# Revit family: LC-3
name_source: partatom
category: Generic Models
revit_build: Autodesk Revit 2017 (Build: 20170419_0315(x64)
units: mm (PartAtom-declared; Revit-internal decimal feet)

## family parameters
Always vertical = Yes
Can host rebar = No
Cut with Voids When Loaded = No
Host = Wall
Part Type = Normal
Room Calculation Point = No
Round Connector Dimension = Use Diameter
Shared = No

## types (3) — shared parameters
Depth = 88 mm
Height = 370 mm  [stored 1.21391 ft]
Keynote = 6120
Manufacturer = Sentakia Oy
Materiaali = kromattu messinki (CuZn36As)
Sentakia_Material_Default = Steel Chrome plated_sentakia

## per-type parameters (varying)
| type | EAN | LVI | Leveys | Model | Teho | URL |
| 350 | 4770046007559 | 5489936 | 350 mm | LC-3/350 | kromi: 45 W maalattu: 58 W | http://www.sentakia.com |
| 500 | 4770046005777 | 5489937 | 500 mm | LC-3/500 | kromi: 55 W maalattu: 71 W | http//:www.sentakia.com |
| 600 | 4770046005692 | 5489938 | 600 mm | LC-3/600 | 58 W | http://www.sentakia.com |

note: [stored X ft] marks values corroborated as IEEE doubles in the binary element streams (Revit-internal decimal feet)

## geometry (parser evidence)
native form markers: Blend x4, Sweep x3
no freeform markers — native parametric forms only
